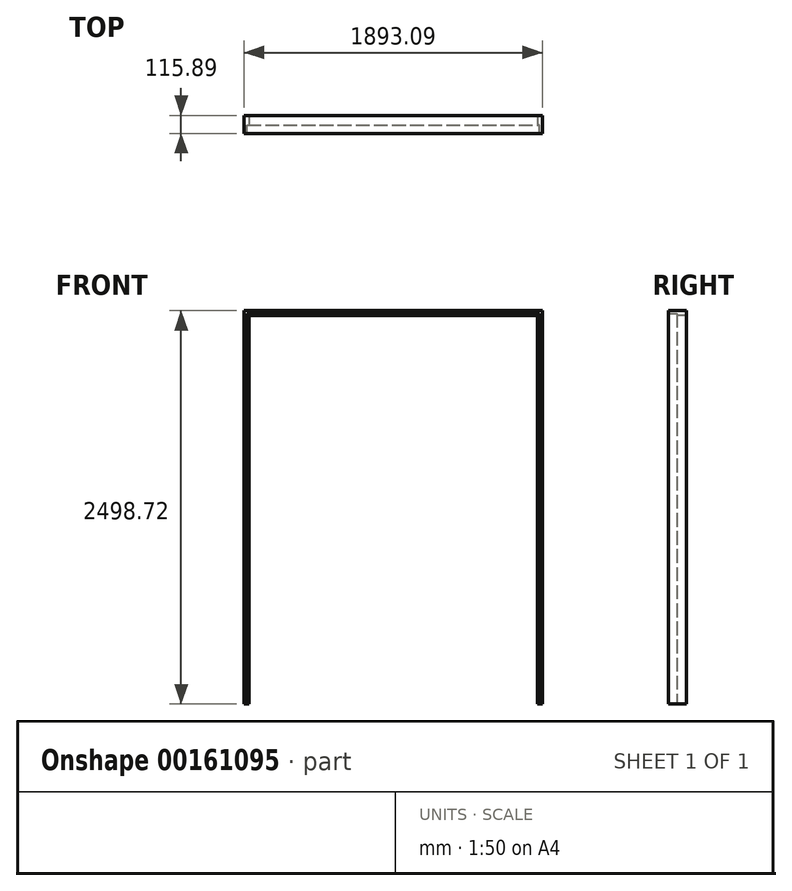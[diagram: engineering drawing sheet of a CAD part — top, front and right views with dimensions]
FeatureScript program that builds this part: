
annotation { "Feature Type Name" : "Feature", "Feature Type Description" : "" }
export const myFeature = defineFeature(function(context is Context, id is Id, definition is map)
    precondition{}
    {
        {
            var Q0;
            Q0=qCreatedBy(makeId("Front.planeOp"),FACE);
            cPlane(context, id + "F0", {"entities" : qUnion([Q0]), "cplaneType" : CPlaneType.OFFSET, "offset" : 3.17 * mm, "oppositeDirection" : true, "width" : 152.4 * mm, "height" : 152.4 * mm});
        }
        {
            var Q0;
            Q0=qCreatedBy(makeId("Front.planeOp"),FACE);
            var sketch = newSketch(context, id + "F1", { "sketchPlane" : qUnion([Q0])});
            skLineSegment(sketch, "E0.bottom", {"start": v(0, 0) * mm, "end": v(19.05, 0) * mm});
            skLineSegment(sketch, "E0.top", {"start": v(0, 2479.68) * mm, "end": v(19.05, 2479.68) * mm});
            skLineSegment(sketch, "E0.left", {"start": v(0, 0) * mm, "end": v(0, 2479.68) * mm});
            skLineSegment(sketch, "E0.right", {"start": v(19.05, 0) * mm, "end": v(19.05, 2479.68) * mm});
            skLineSegment(sketch, "E1.bottom", {"start": v(31.75, 2466.98) * mm, "end": v(19.05, 2466.98) * mm});
            skLineSegment(sketch, "E1.top", {"start": v(31.75, 0) * mm, "end": v(19.05, 0) * mm});
            skLineSegment(sketch, "E1.left", {"start": v(31.75, 2466.97) * mm, "end": v(31.75, 0) * mm});
            skLineSegment(sketch, "E1.right", {"start": v(19.05, 2466.97) * mm, "end": v(19.05, 0) * mm});
            skLineSegment(sketch, "E2.bottom", {"start": v(0, 2479.68) * mm, "end": v(1893.1, 2479.68) * mm});
            skLineSegment(sketch, "E2.top", {"start": v(0, 2498.73) * mm, "end": v(1893.1, 2498.73) * mm});
            skLineSegment(sketch, "E2.left", {"start": v(0, 2479.68) * mm, "end": v(0, 2498.73) * mm});
            skLineSegment(sketch, "E2.right", {"start": v(1893.1, 2479.68) * mm, "end": v(1893.1, 2498.73) * mm});
            skPoint(sketch, "E3.oppositeSnap0", {"position": v(9.53, 0) * mm});
            skLineSegment(sketch, "E3.bottom", {"start": v(1893.1, 2479.68) * mm, "end": v(1874.04, 2479.68) * mm});
            skLineSegment(sketch, "E3.top", {"start": v(1893.1, 0) * mm, "end": v(1874.04, 0) * mm});
            skLineSegment(sketch, "E3.left", {"start": v(1893.1, 2479.68) * mm, "end": v(1893.1, 0) * mm});
            skLineSegment(sketch, "E3.right", {"start": v(1874.04, 2479.68) * mm, "end": v(1874.04, 0) * mm});
            skLineSegment(sketch, "E4.bottom", {"start": v(1874.04, 0) * mm, "end": v(1861.34, 0) * mm});
            skLineSegment(sketch, "E4.top", {"start": v(1874.04, 2466.98) * mm, "end": v(1861.34, 2466.98) * mm});
            skLineSegment(sketch, "E4.left", {"start": v(1874.04, 0) * mm, "end": v(1874.04, 2466.98) * mm});
            skLineSegment(sketch, "E4.right", {"start": v(1861.34, 0) * mm, "end": v(1861.34, 2466.98) * mm});
            skLineSegment(sketch, "E5.bottom", {"start": v(19.05, 2479.68) * mm, "end": v(1874.04, 2479.68) * mm});
            skLineSegment(sketch, "E5.left", {"start": v(19.05, 2479.68) * mm, "end": v(19.05, 2466.98) * mm});
            skLineSegment(sketch, "E5.right", {"start": v(1874.04, 2479.68) * mm, "end": v(1874.04, 2466.98) * mm});
            skLineSegment(sketch, "E6.bottom", {"start": v(19.05, 2479.68) * mm, "end": v(593.72, 2479.68) * mm});
            skLineSegment(sketch, "E6.left", {"start": v(19.05, 2479.68) * mm, "end": v(19.05, 2466.97) * mm});
            skLineSegment(sketch, "E7", {"start": v(31.75, 2466.97) * mm, "end": v(1861.34, 2466.98) * mm});
            skSolve(sketch);
        }
        {
            var Q0;
            Q0=qCreatedBy(id+"F0.planeOp",FACE);
            var sketch = newSketch(context, id + "F2", { "sketchPlane" : qUnion([Q0])});
            skLineSegment(sketch, "E8.0", {"start": v(0, 0) * mm, "end": v(0, 2479.68) * mm});
            skLineSegment(sketch, "E9.0", {"start": v(0, 0) * mm, "end": v(19.05, 0) * mm});
            skLineSegment(sketch, "E10.0", {"start": v(31.75, 0) * mm, "end": v(19.05, 0) * mm});
            skLineSegment(sketch, "E11.0", {"start": v(31.75, 2466.97) * mm, "end": v(31.75, 0) * mm});
            skLineSegment(sketch, "E12.0", {"start": v(0, 2498.73) * mm, "end": v(1893.1, 2498.73) * mm});
            skLineSegment(sketch, "E13.0", {"start": v(0, 2479.68) * mm, "end": v(0, 2498.73) * mm});
            skLineSegment(sketch, "E14.0", {"start": v(1861.34, 0) * mm, "end": v(1861.34, 2466.98) * mm});
            skLineSegment(sketch, "E15.0", {"start": v(1893.1, 2479.68) * mm, "end": v(1893.1, 0) * mm});
            skLineSegment(sketch, "E16.0", {"start": v(1893.1, 2479.68) * mm, "end": v(1893.1, 2498.73) * mm});
            skLineSegment(sketch, "E17.0", {"start": v(1874.04, 0) * mm, "end": v(1861.34, 0) * mm});
            skLineSegment(sketch, "E18.0", {"start": v(1893.1, 0) * mm, "end": v(1874.04, 0) * mm});
            skLineSegment(sketch, "E19.0", {"start": v(31.75, 2466.97) * mm, "end": v(1861.34, 2466.98) * mm});
            skSolve(sketch);
        }
        {
            var Q0;
            Q0=qSketchRegion(id+"F2",true);
            extrude(context, id + "F3", {"entities" : qUnion([Q0]), "oppositeDirection" : true, "depth" : 61.9 * mm});
        }
        {
            var Q0;
            Q0=qCreatedBy(makeId("Front.planeOp"),FACE);
            var sketch = newSketch(context, id + "F4", { "sketchPlane" : qUnion([Q0])});
            skLineSegment(sketch, "E20.0", {"start": v(0, 0) * mm, "end": v(19.05, 0) * mm});
            skLineSegment(sketch, "E21.0", {"start": v(19.05, 2466.97) * mm, "end": v(19.05, 0) * mm});
            skLineSegment(sketch, "E22.0", {"start": v(0, 0) * mm, "end": v(0, 2479.68) * mm});
            skLineSegment(sketch, "E23.0", {"start": v(0, 2479.68) * mm, "end": v(0, 2498.73) * mm});
            skLineSegment(sketch, "E24.0", {"start": v(0, 2498.73) * mm, "end": v(1893.1, 2498.73) * mm});
            skLineSegment(sketch, "E25.0", {"start": v(19.05, 2479.68) * mm, "end": v(19.05, 2466.97) * mm});
            skLineSegment(sketch, "E26.0", {"start": v(19.05, 2479.68) * mm, "end": v(593.72, 2479.68) * mm});
            skLineSegment(sketch, "E27.0", {"start": v(1874.04, 2479.68) * mm, "end": v(1874.04, 2466.98) * mm});
            skLineSegment(sketch, "E28.0", {"start": v(1874.04, 0) * mm, "end": v(1874.04, 2466.98) * mm});
            skLineSegment(sketch, "E29.0", {"start": v(1893.1, 2479.68) * mm, "end": v(1893.1, 0) * mm});
            skPoint(sketch, "E30.0", {"position": v(1893.1, 2489.2) * mm});
            skLineSegment(sketch, "E31.0", {"start": v(1893.1, 2479.68) * mm, "end": v(1893.1, 2498.73) * mm});
            skLineSegment(sketch, "E32", {"start": v(1299.37, 2479.68) * mm, "end": v(1874.04, 2479.68) * mm});
            skLineSegment(sketch, "E33.0", {"start": v(1893.1, 0) * mm, "end": v(1874.04, 0) * mm});
            skLineSegment(sketch, "E34", {"start": v(593.72, 2479.68) * mm, "end": v(1874.04, 2479.68) * mm});
            skSolve(sketch);
        }
        {
            var Q0;
            Q0=qSketchRegion(id+"F4",true);
            extrude(context, id + "F5", {"entities" : qUnion([Q0]), "operationType" : NewBodyOperationType.ADD, "depth" : 50.8 * mm, "hasSecondDirection" : true, "secondDirectionOppositeDirection" : true, "secondDirectionDepth" : 3.17 * mm});
        }
    });
